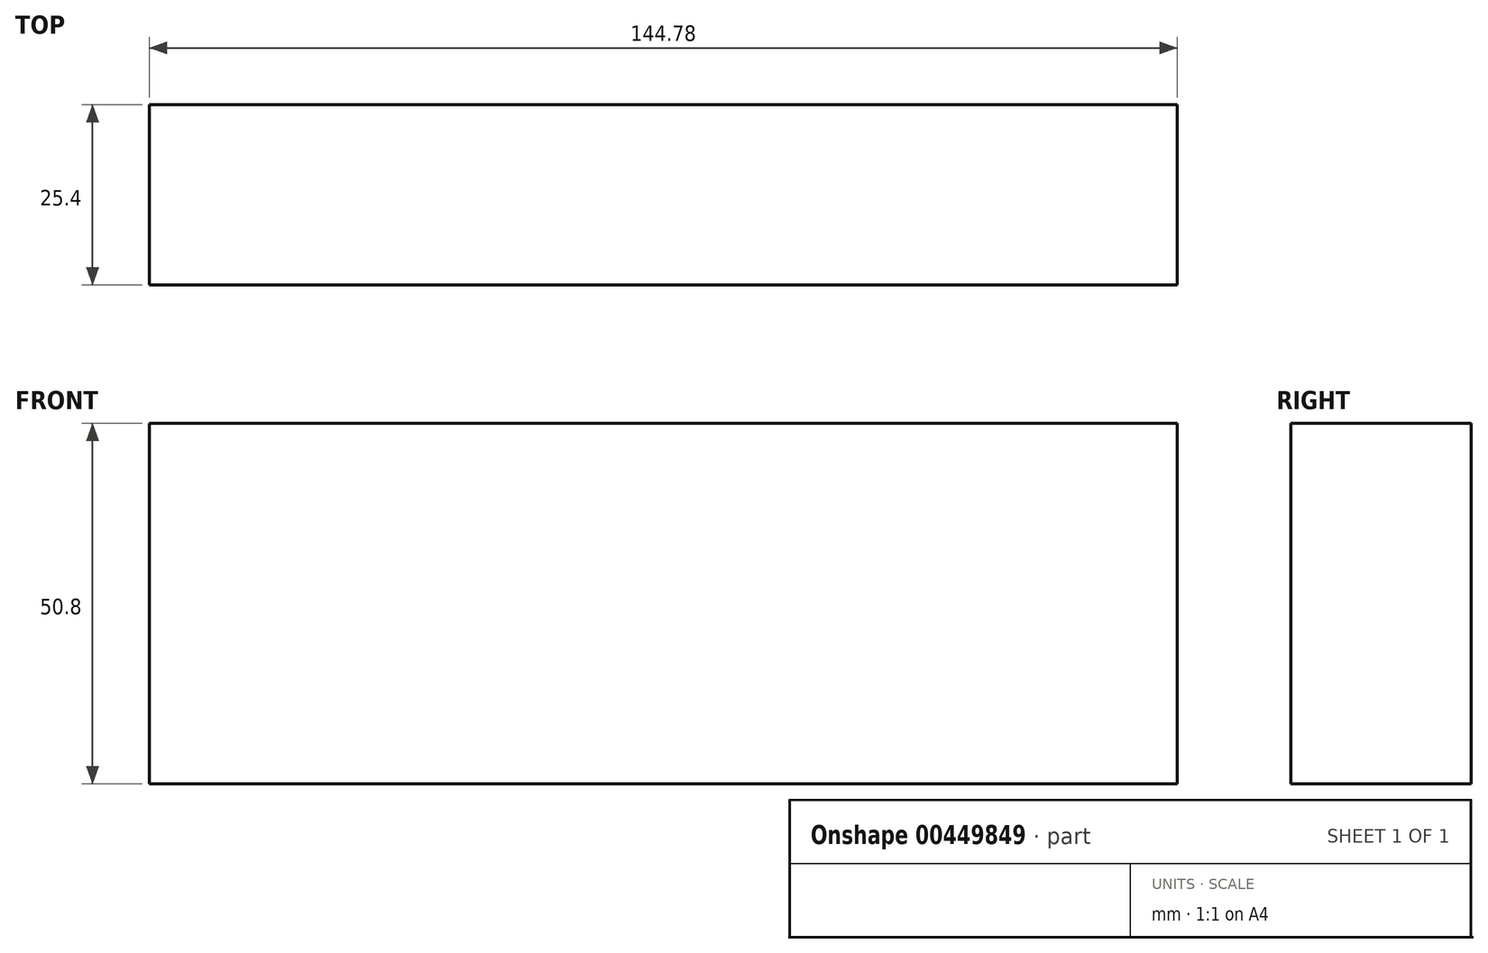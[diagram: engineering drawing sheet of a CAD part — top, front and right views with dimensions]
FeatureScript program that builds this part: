
annotation { "Feature Type Name" : "Feature", "Feature Type Description" : "" }
export const myFeature = defineFeature(function(context is Context, id is Id, definition is map)
    precondition{}
    {
        {
            var Q0;
            Q0=qCreatedBy(makeId("Front.planeOp"),FACE);
            var sketch = newSketch(context, id + "F0", { "sketchPlane" : qUnion([Q0])});
            skLineSegment(sketch, "E0.bottom", {"start": v(-135.66, 51.53) * mm, "end": v(9.12, 51.53) * mm});
            skLineSegment(sketch, "E0.top", {"start": v(-135.66, 0.73) * mm, "end": v(9.12, 0.73) * mm});
            skLineSegment(sketch, "E0.left", {"start": v(-135.66, 51.53) * mm, "end": v(-135.66, 0.73) * mm});
            skLineSegment(sketch, "E0.right", {"start": v(9.12, 51.53) * mm, "end": v(9.12, 0.73) * mm});
            skSolve(sketch);
        }
        {
            var Q0;
            Q0=makeQuery(id+"F0.imprint","IMPRINT",FACE,{"disambiguationData":[TD([[makeQuery(id+"F0.imprint","IMPRINT",EDGE,{"derivedFrom":sQuery(id+"F0.wireOp",EDGE,"E0.bottom")}),-1.0]])]});
            extrude(context, id + "F1", {"entities" : qUnion([Q0]), "depth" : 25.4 * mm});
        }
    });
